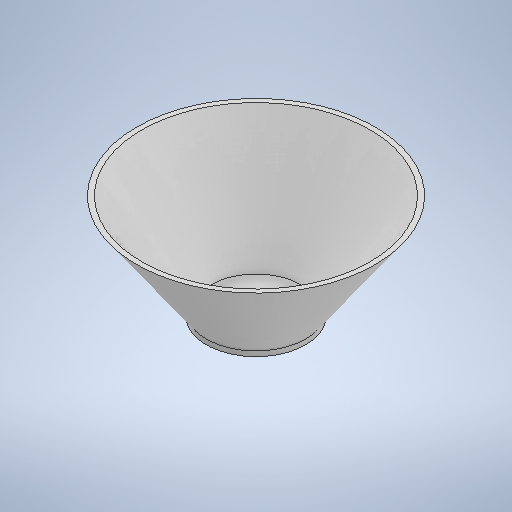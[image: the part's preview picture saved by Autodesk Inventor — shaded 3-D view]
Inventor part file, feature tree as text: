
AUTODESK INVENTOR PART (.ipt)
format: ipt  version: 2025 (Build 290162000, 162)  size: 270,848 bytes
history: native  units: mm
features: extrude x5, sketch x5
ambient origin geometry x8: Origin, YZ Plane, XZ Plane, XY Plane, X Axis, Y Axis, Z Axis, Center Point
bodies: Body1 (feature_tree)
feature tree (10):
  extrude  "Wyciągnięcie proste5"  Depth=100.0mm
  extrude  "Wyciągnięcie proste6"  Depth=100.0mm
  extrude  "Wyciągnięcie proste7"  Depth=90.0mm
  extrude  "Wyciągnięcie proste8"  Depth=100.0mm
  extrude  "Wyciągnięcie proste9"  Depth=5.0mm TaperAngle=0.0deg
  sketch  "Szkic6"
  sketch  "Szkic7"
  sketch  "Szkic8"
  sketch  "Szkic9"
  sketch  "Szkic10"
